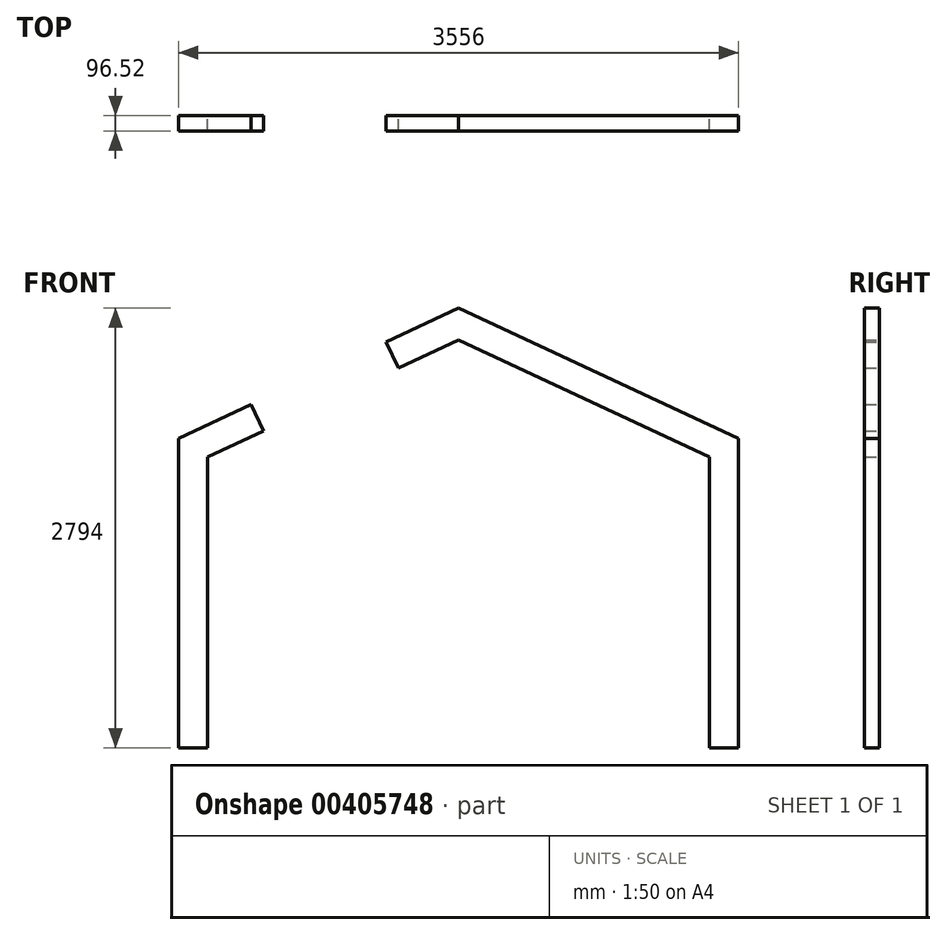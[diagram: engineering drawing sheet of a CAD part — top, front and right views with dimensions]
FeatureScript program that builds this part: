
annotation { "Feature Type Name" : "Feature", "Feature Type Description" : "" }
export const myFeature = defineFeature(function(context is Context, id is Id, definition is map)
    precondition{}
    {
        {
            var Q0;
            Q0=qCreatedBy(makeId("Front.planeOp"),FACE);
            var sketch = newSketch(context, id + "F0", { "sketchPlane" : qUnion([Q0])});
            skLineSegment(sketch, "E0.bottom", {"start": v(-1592.58, 0) * mm, "end": v(-1778, 0) * mm});
            skLineSegment(sketch, "E0.top", {"start": v(-1592.58, 1846.78) * mm, "end": v(-1778, 1846.78) * mm});
            skLineSegment(sketch, "E0.left", {"start": v(-1592.58, 0) * mm, "end": v(-1592.58, 1846.78) * mm});
            skLineSegment(sketch, "E0.right", {"start": v(-1778, 0) * mm, "end": v(-1778, 1964.9) * mm});
            skLineSegment(sketch, "E1.bottom", {"start": v(-1592.58, 1846.78) * mm, "end": v(0, 2589.41) * mm});
            skLineSegment(sketch, "E1.top", {"start": v(-1778, 1964.9) * mm, "end": v(0, 2794) * mm});
            skLineSegment(sketch, "E1.left", {"start": v(-1592.58, 1846.78) * mm, "end": v(-1670.94, 2014.83) * mm});
            skLineSegment(sketch, "E1.right", {"start": v(0, 2589.41) * mm, "end": v(-78.36, 2757.46) * mm});
            skLineSegment(sketch, "E2", {"start": v(-1592.58, 1846.78) * mm, "end": v(-1778, 1964.9) * mm});
            skLineSegment(sketch, "E3", {"start": v(-1778, 1964.9) * mm, "end": v(-1317.6, 2179.6) * mm});
            skLineSegment(sketch, "E4", {"start": v(-1317.6, 2179.6) * mm, "end": v(-1239.23, 2011.55) * mm});
            skLineSegment(sketch, "E5", {"start": v(-1239.23, 2011.55) * mm, "end": v(-1592.58, 1456.9) * mm});
            skLineSegment(sketch, "E6", {"start": v(-1592.58, 1456.9) * mm, "end": v(-1778, 1456.9) * mm});
            skLineSegment(sketch, "E7", {"start": v(-1778, 1456.9) * mm, "end": v(-1778, 1964.9) * mm});
            skLineSegment(sketch, "E8.MirrorCS", {"start": v(0, 2589.41) * mm, "end": v(78.36, 2757.46) * mm});
            skLineSegment(sketch, "E9.MirrorCS", {"start": v(1778, 1456.9) * mm, "end": v(1778, 1964.9) * mm});
            skLineSegment(sketch, "E10.MirrorCS", {"start": v(1592.58, 0) * mm, "end": v(1778, 0) * mm});
            skLineSegment(sketch, "E11.MirrorCS", {"start": v(1592.58, 1846.78) * mm, "end": v(1778, 1846.78) * mm});
            skLineSegment(sketch, "E12.MirrorCS", {"start": v(1592.58, 0) * mm, "end": v(1592.58, 1846.78) * mm});
            skLineSegment(sketch, "E13.MirrorCS", {"start": v(1778, 0) * mm, "end": v(1778, 1964.9) * mm});
            skLineSegment(sketch, "E14.MirrorCS", {"start": v(1592.58, 1846.78) * mm, "end": v(0, 2589.41) * mm});
            skLineSegment(sketch, "E15.MirrorCS", {"start": v(1317.6, 2179.6) * mm, "end": v(1239.23, 2011.55) * mm});
            skLineSegment(sketch, "E16.MirrorCS", {"start": v(1592.58, 1456.9) * mm, "end": v(1778, 1456.9) * mm});
            skLineSegment(sketch, "E17.MirrorCS", {"start": v(1778, 1964.9) * mm, "end": v(0, 2794) * mm});
            skLineSegment(sketch, "E18.MirrorCS", {"start": v(1592.58, 1846.78) * mm, "end": v(1778, 1964.9) * mm});
            skLineSegment(sketch, "E19.MirrorCS", {"start": v(1239.23, 2011.55) * mm, "end": v(1592.58, 1456.9) * mm});
            skLineSegment(sketch, "E20.MirrorCS", {"start": v(1778, 1964.9) * mm, "end": v(1317.6, 2179.6) * mm});
            skLineSegment(sketch, "E21.MirrorCS", {"start": v(1592.58, 1846.78) * mm, "end": v(1670.94, 2014.83) * mm});
            skLineSegment(sketch, "E22", {"start": v(0, 2794) * mm, "end": v(0, 2589.41) * mm});
            skLineSegment(sketch, "E23", {"start": v(0, 2794) * mm, "end": v(-460.4, 2579.3) * mm});
            skLineSegment(sketch, "E24", {"start": v(-460.4, 2579.3) * mm, "end": v(-382.04, 2411.26) * mm});
            skLineSegment(sketch, "E25", {"start": v(-382.04, 2411.26) * mm, "end": v(382.04, 2411.26) * mm});
            skLineSegment(sketch, "E26", {"start": v(382.04, 2411.26) * mm, "end": v(460.4, 2579.3) * mm});
            skLineSegment(sketch, "E27", {"start": v(460.4, 2579.3) * mm, "end": v(0, 2794) * mm});
            skSolve(sketch);
        }
        {
            var Q0;
            {var subQ0=sQuery(id+"F0.wireOp",EDGE,"E11.MirrorCS");Q0=makeQuery(id+"F0.imprint","IMPRINT",FACE,{"disambiguationData":[TD([[makeQuery(id+"F0.imprint","IMPRINT",EDGE,{"derivedFrom":subQ0}),-1.0]])]});}
            var Q1;
            {var subQ0=sQuery(id+"F0.wireOp",EDGE,"E18.MirrorCS");Q1=makeQuery(id+"F0.imprint","IMPRINT",FACE,{"disambiguationData":[TD([[makeQuery(id+"F0.imprint","IMPRINT",EDGE,{"derivedFrom":subQ0}),1.0]])]});}
            var Q2;
            {var subQ0=sQuery(id+"F0.wireOp",EDGE,"E15.MirrorCS");Q2=makeQuery(id+"F0.imprint","IMPRINT",FACE,{"disambiguationData":[TD([[makeQuery(id+"F0.imprint","IMPRINT",EDGE,{"derivedFrom":subQ0}),-1.0]])]});}
            var Q3;
            {var subQ0=sQuery(id+"F0.wireOp",EDGE,"E1.left");Q3=makeQuery(id+"F0.imprint","IMPRINT",FACE,{"disambiguationData":[TD([[makeQuery(id+"F0.imprint","IMPRINT",EDGE,{"derivedFrom":subQ0}),1.0]])]});}
            var Q4;
            {var subQ0=sQuery(id+"F0.wireOp",EDGE,"E0.bottom");Q4=makeQuery(id+"F0.imprint","IMPRINT",FACE,{"disambiguationData":[TD([[makeQuery(id+"F0.imprint","IMPRINT",EDGE,{"derivedFrom":subQ0}),-1.0]])]});}
            var Q5;
            {var subQ2=sQuery(id+"F0.wireOp",EDGE,"E15.MirrorCS");Q5=makeQuery(id+"F0.imprint","IMPRINT",FACE,{"disambiguationData":[TD([[makeQuery(id+"F0.imprint","IMPRINT",EDGE,{"derivedFrom":subQ2}),1.0]])]});}
            var Q6;
            {var subQ0=sQuery(id+"F0.wireOp",EDGE,"E10.MirrorCS");Q6=makeQuery(id+"F0.imprint","IMPRINT",FACE,{"disambiguationData":[TD([[makeQuery(id+"F0.imprint","IMPRINT",EDGE,{"derivedFrom":subQ0}),1.0]])]});}
            var Q7;
            {var subQ0=sQuery(id+"F0.wireOp",EDGE,"E1.left");Q7=makeQuery(id+"F0.imprint","IMPRINT",FACE,{"disambiguationData":[TD([[makeQuery(id+"F0.imprint","IMPRINT",EDGE,{"derivedFrom":subQ0}),-1.0]])]});}
            var Q8;
            {var subQ0=sQuery(id+"F0.wireOp",EDGE,"E8.MirrorCS");Q8=makeQuery(id+"F0.imprint","IMPRINT",FACE,{"disambiguationData":[TD([[makeQuery(id+"F0.imprint","IMPRINT",EDGE,{"derivedFrom":subQ0}),-1.0]])]});}
            var Q9;
            {var subQ0=sQuery(id+"F0.wireOp",EDGE,"E0.top");Q9=makeQuery(id+"F0.imprint","IMPRINT",FACE,{"disambiguationData":[TD([[makeQuery(id+"F0.imprint","IMPRINT",EDGE,{"derivedFrom":subQ0}),1.0]])]});}
            var Q10;
            {var subQ0=sQuery(id+"F0.wireOp",EDGE,"E1.right");Q10=makeQuery(id+"F0.imprint","IMPRINT",FACE,{"disambiguationData":[TD([[makeQuery(id+"F0.imprint","IMPRINT",EDGE,{"derivedFrom":subQ0}),1.0]])]});}
            var Q11;
            {var subQ0=sQuery(id+"F0.wireOp",EDGE,"E1.right");Q11=makeQuery(id+"F0.imprint","IMPRINT",FACE,{"disambiguationData":[TD([[makeQuery(id+"F0.imprint","IMPRINT",EDGE,{"derivedFrom":subQ0}),-1.0]])]});}
            var Q12;
            {var subQ0=sQuery(id+"F0.wireOp",EDGE,"E0.top");Q12=makeQuery(id+"F0.imprint","IMPRINT",FACE,{"disambiguationData":[TD([[makeQuery(id+"F0.imprint","IMPRINT",EDGE,{"derivedFrom":subQ0}),-1.0]])]});}
            var Q13;
            {var subQ0=sQuery(id+"F0.wireOp",EDGE,"E11.MirrorCS");Q13=makeQuery(id+"F0.imprint","IMPRINT",FACE,{"disambiguationData":[TD([[makeQuery(id+"F0.imprint","IMPRINT",EDGE,{"derivedFrom":subQ0}),1.0]])]});}
            var Q14;
            Q14=makeQuery(id+"F0.imprint","IMPRINT",FACE,{"disambiguationData":[TD([[makeQuery(id+"F0.imprint","IMPRINT",EDGE,{"derivedFrom":sQuery(id+"F0.wireOp",EDGE,"E1.top")}),-1.0]])]});
            var Q15;
            {var subQ0=sQuery(id+"F0.wireOp",EDGE,"E8.MirrorCS");Q15=makeQuery(id+"F0.imprint","IMPRINT",FACE,{"disambiguationData":[TD([[makeQuery(id+"F0.imprint","IMPRINT",EDGE,{"derivedFrom":subQ0}),1.0]])]});}
            extrude(context, id + "F1", {"entities" : qUnion([Q0, Q1, Q2, Q3, Q4, Q5, Q6, Q7, Q8, Q9, Q10, Q11, Q12, Q13, Q14, Q15]), "depth" : 96.52 * mm});
        }
    });
